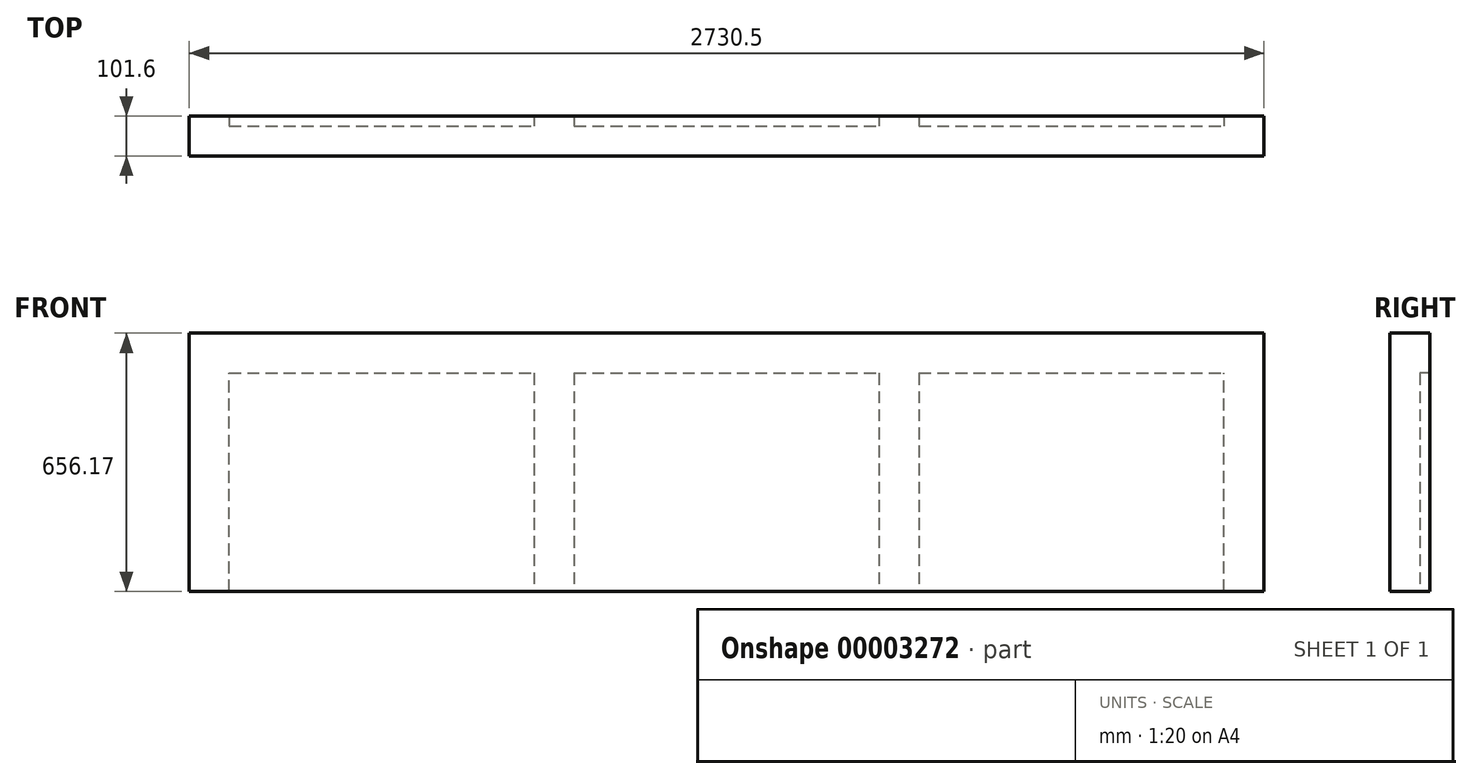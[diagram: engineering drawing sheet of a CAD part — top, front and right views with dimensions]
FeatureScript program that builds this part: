
annotation { "Feature Type Name" : "Feature", "Feature Type Description" : "" }
export const myFeature = defineFeature(function(context is Context, id is Id, definition is map)
    precondition{}
    {
        {
            var Q0;
            Q0=qCreatedBy(makeId("Front.planeOp"),FACE);
            var sketch = newSketch(context, id + "F0", { "sketchPlane" : qUnion([Q0])});
            skLineSegment(sketch, "E0.bottom", {"start": v(0, 0) * mm, "end": v(2730.5, 0) * mm});
            skLineSegment(sketch, "E0.top", {"start": v(0, 656.17) * mm, "end": v(2730.5, 656.17) * mm});
            skLineSegment(sketch, "E0.left", {"start": v(0, 0) * mm, "end": v(0, 656.17) * mm});
            skLineSegment(sketch, "E0.right", {"start": v(2730.5, 0) * mm, "end": v(2730.5, 656.17) * mm});
            skSolve(sketch);
        }
        {
            var Q0;
            Q0=makeQuery(id+"F0.imprint","IMPRINT",FACE,{"disambiguationData":[TD([[makeQuery(id+"F0.imprint","IMPRINT",EDGE,{"derivedFrom":sQuery(id+"F0.wireOp",EDGE,"E0.bottom")}),1.0]])]});
            extrude(context, id + "F1", {"entities" : qUnion([Q0]), "depth" : 76.2 * mm});
        }
        {
            var Q0;
            Q0=makeQuery(id+"F1.opExtrude","CAP_FACE",FACE,{"disambiguationData":[OSD([sQuery(id+"F0.wireOp",EDGE,"E0.bottom"),sQuery(id+"F0.wireOp",EDGE,"E0.top"),sQuery(id+"F0.wireOp",EDGE,"E0.left"),sQuery(id+"F0.wireOp",EDGE,"E0.right")])],"isStart":true});
            var sketch = newSketch(context, id + "F2", { "sketchPlane" : qUnion([Q0])});
            skLineSegment(sketch, "E1.1", {"start": v(0, 0) * mm, "end": v(0, 656.17) * mm});
            skLineSegment(sketch, "E1.2", {"start": v(0, 656.17) * mm, "end": v(-2730.5, 656.17) * mm, "construction": true});
            skLineSegment(sketch, "E1.3", {"start": v(-2730.5, 0) * mm, "end": v(-2730.5, 656.17) * mm});
            skLineSegment(sketch, "E2.0", {"start": v(-101.6, 0) * mm, "end": v(-101.6, 554.57) * mm});
            skLineSegment(sketch, "E2.1", {"start": v(-101.6, 554.57) * mm, "end": v(-876.3, 554.57) * mm});
            skLineSegment(sketch, "E2.2", {"start": v(-2628.9, 0) * mm, "end": v(-2628.9, 554.57) * mm});
            skPoint(sketch, "E3", {"position": v(-1803.4, 656.17) * mm});
            skPoint(sketch, "E4", {"position": v(0, 656.17) * mm});
            skLineSegment(sketch, "E5", {"start": v(-2730.5, 656.17) * mm, "end": v(-1803.4, 656.17) * mm});
            skLineSegment(sketch, "E6", {"start": v(-1803.4, 656.17) * mm, "end": v(0, 656.17) * mm});
            skLineSegment(sketch, "E7", {"start": v(0, 656.17) * mm, "end": v(0, 656.17) * mm});
            skLineSegment(sketch, "E8", {"start": v(-1803.4, 656.17) * mm, "end": v(-1803.4, 0) * mm, "construction": true});
            skLineSegment(sketch, "E9", {"start": v(-1854.2, 554.57) * mm, "end": v(-1854.2, 0) * mm});
            skPoint(sketch, "E10.0.MirrorP", {"position": v(-3606.8, 656.17) * mm});
            skLineSegment(sketch, "E11.0.MirrorCS", {"start": v(-1752.6, 554.57) * mm, "end": v(-1752.6, 0) * mm});
            skLineSegment(sketch, "E12.trimOffspring", {"start": v(-1854.2, 554.57) * mm, "end": v(-2628.9, 554.57) * mm});
            skPoint(sketch, "E13", {"position": v(-1365.25, 656.17) * mm});
            skLineSegment(sketch, "E14", {"start": v(-1365.25, 656.17) * mm, "end": v(-1365.25, 0) * mm, "construction": true});
            skLineSegment(sketch, "E15.0.MirrorCS", {"start": v(-977.9, 554.57) * mm, "end": v(-977.9, 0) * mm});
            skLineSegment(sketch, "E16.0.MirrorCS", {"start": v(-876.3, 554.57) * mm, "end": v(-876.3, 0) * mm});
            skLineSegment(sketch, "E17.trimOffspring", {"start": v(-977.9, 554.57) * mm, "end": v(-1752.6, 554.57) * mm});
            skLineSegment(sketch, "E18", {"start": v(-2730.5, 0) * mm, "end": v(-2628.9, 0) * mm});
            skLineSegment(sketch, "E19", {"start": v(-1854.2, 0) * mm, "end": v(-1752.6, 0) * mm});
            skLineSegment(sketch, "E20", {"start": v(-977.9, 0) * mm, "end": v(-876.3, 0) * mm});
            skLineSegment(sketch, "E21", {"start": v(-101.6, 0) * mm, "end": v(0, 0) * mm});
            skSolve(sketch);
        }
        {
            var Q0;
            Q0 = qSketchRegion(id + "F2", true);
            extrude(context, id + "F3", {"entities" : qUnion([Q0]), "operationType" : NewBodyOperationType.ADD, "depth" : 25.4 * mm});
        }
    });
